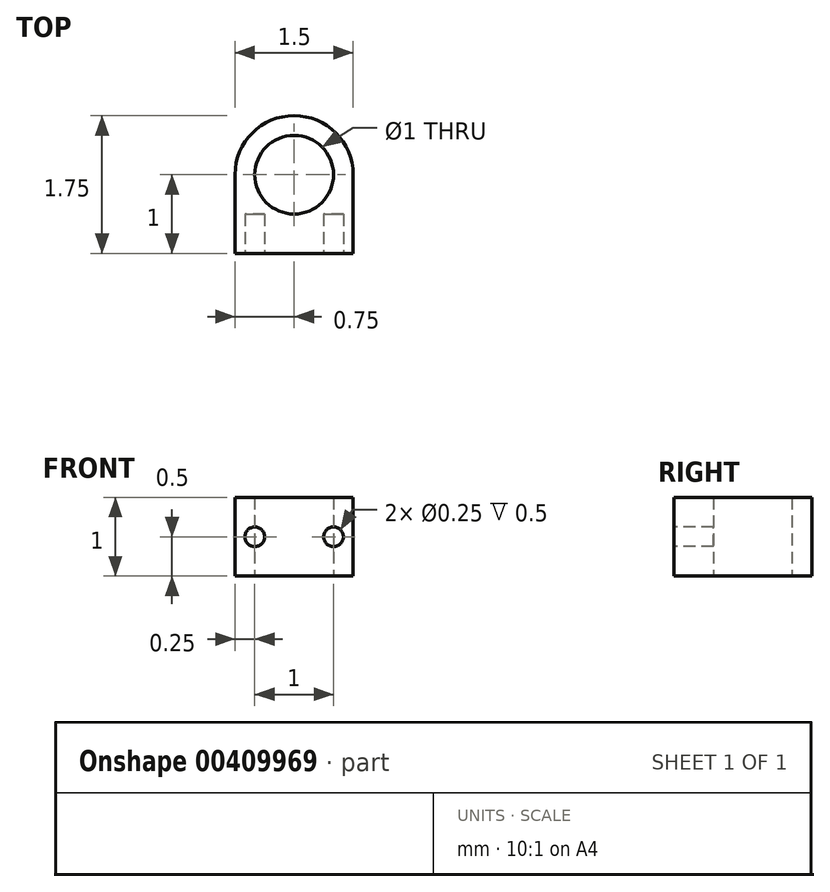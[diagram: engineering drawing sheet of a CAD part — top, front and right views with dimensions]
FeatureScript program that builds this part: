
annotation { "Feature Type Name" : "Feature", "Feature Type Description" : "" }
export const myFeature = defineFeature(function(context is Context, id is Id, definition is map)
    precondition{}
    {
        {
            var Q0;
            Q0=qCreatedBy(makeId("Top.planeOp"),FACE);
            var sketch = newSketch(context, id + "F0", { "sketchPlane" : qUnion([Q0])});
            skCircle(sketch, "E0", {"center": v(0, 0) * mm, "radius": 0.5 * mm});
            skArc(sketch, "E1", {"start": v(0.75, 0) * mm, "mid": v(0, 0.75) * mm, "end": v(-0.75, 0) * mm});
            skLineSegment(sketch, "E2.top", {"start": v(-0.75, -1) * mm, "end": v(0.75, -1) * mm});
            skLineSegment(sketch, "E2.left", {"start": v(-0.75, 0) * mm, "end": v(-0.75, -1) * mm});
            skLineSegment(sketch, "E2.right", {"start": v(0.75, 0) * mm, "end": v(0.75, -1) * mm});
            skSolve(sketch);
        }
        {
            var Q0;
            Q0 = qSketchRegion(id + "F0", true);
            extrude(context, id + "F1", {"entities" : qUnion([Q0]), "depth" : 1 * mm});
        }
        {
            var Q0;
            Q0=makeQuery(id+"F1.opExtrude","SWEPT_FACE",FACE,{"disambiguationData":[OSD([sQuery(id+"F0.wireOp",EDGE,"E2.top")])]});
            var sketch = newSketch(context, id + "F2", { "sketchPlane" : qUnion([Q0])});
            skLineSegment(sketch, "E3", {"start": v(0.75, 0.5) * mm, "end": v(-1.63, 0.5) * mm, "construction": true});
            skCircle(sketch, "E4", {"center": v(0.5, 0.5) * mm, "radius": 0.12 * mm});
            skCircle(sketch, "E5", {"center": v(-0.5, 0.5) * mm, "radius": 0.12 * mm});
            skSolve(sketch);
        }
        {
            var Q0;
            Q0 = qSketchRegion(id + "F2", true);
            extrude(context, id + "F3", {"entities" : qUnion([Q0]), "operationType" : NewBodyOperationType.REMOVE, "oppositeDirection" : true, "depth" : 0.5 * mm});
        }
    });
